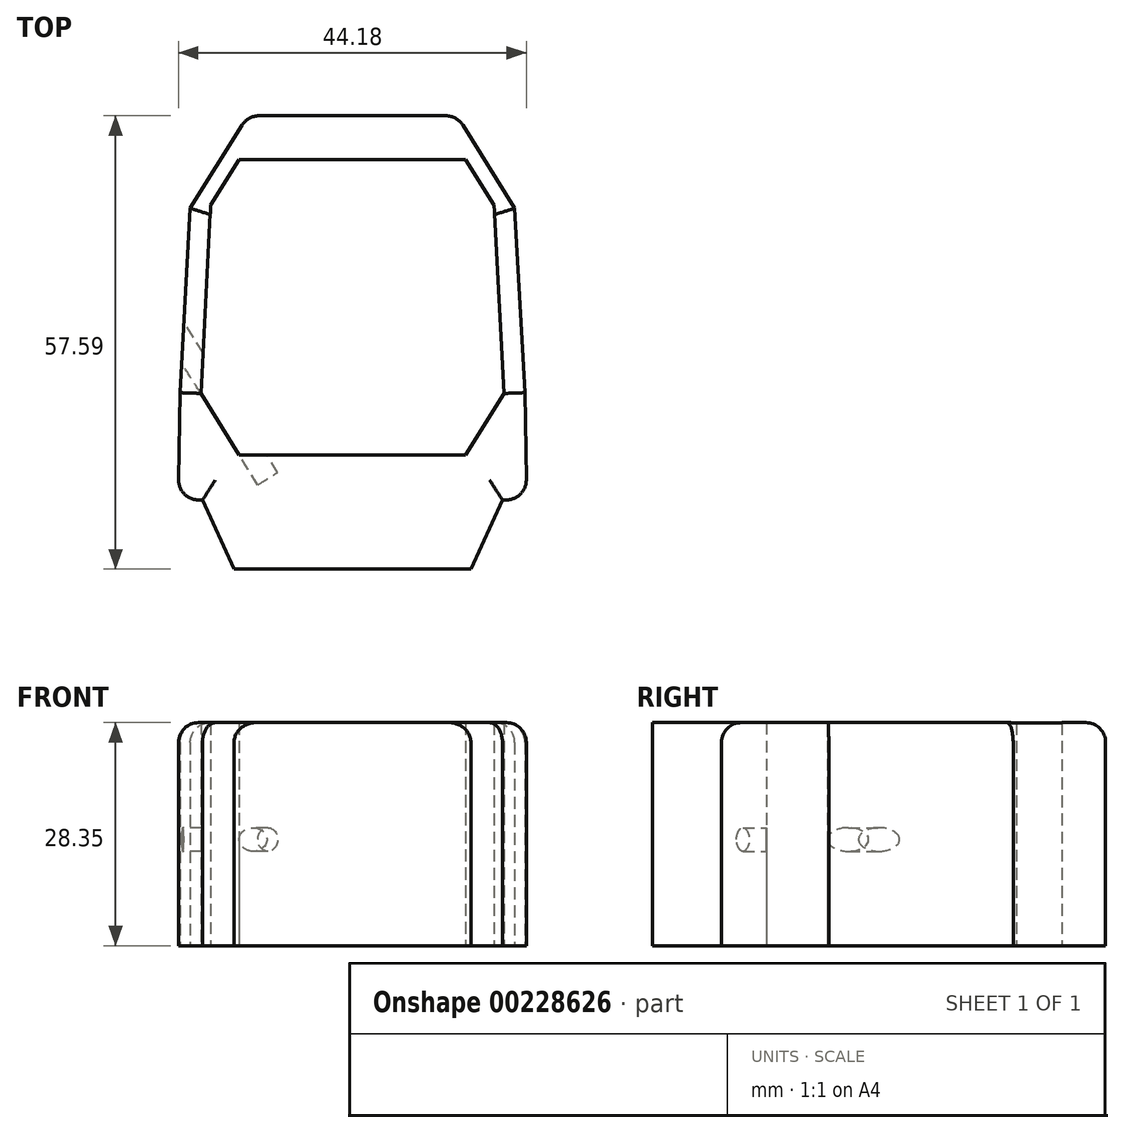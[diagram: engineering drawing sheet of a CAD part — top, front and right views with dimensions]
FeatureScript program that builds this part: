
annotation { "Feature Type Name" : "Feature", "Feature Type Description" : "" }
export const myFeature = defineFeature(function(context is Context, id is Id, definition is map)
    precondition{}
    {
        {
            var Q0;
            Q0=qCreatedBy(makeId("Top.planeOp"),FACE);
            var sketch = newSketch(context, id + "F0", { "sketchPlane" : qUnion([Q0])});
            skLineSegment(sketch, "E0", {"start": v(-14.4, -18.75) * mm, "end": v(14.4, -18.75) * mm});
            skLineSegment(sketch, "E1", {"start": v(14.4, -18.75) * mm, "end": v(19.25, -10.98) * mm});
            skLineSegment(sketch, "E2", {"start": v(19.25, -10.98) * mm, "end": v(18, 12.99) * mm});
            skLineSegment(sketch, "E3", {"start": v(18, 12.99) * mm, "end": v(14.4, 18.75) * mm});
            skLineSegment(sketch, "E4", {"start": v(14.4, 18.75) * mm, "end": v(-14.4, 18.75) * mm});
            skLineSegment(sketch, "E5", {"start": v(-14.4, 18.75) * mm, "end": v(-18, 12.99) * mm});
            skLineSegment(sketch, "E6", {"start": v(-18, 12.99) * mm, "end": v(-19.25, -10.98) * mm});
            skLineSegment(sketch, "E7", {"start": v(-19.25, -10.98) * mm, "end": v(-14.4, -18.75) * mm});
            skLineSegment(sketch, "E8", {"start": v(-15.04, -33.25) * mm, "end": v(15.04, -33.25) * mm});
            skLineSegment(sketch, "E9", {"start": v(22.13, -24.46) * mm, "end": v(21.92, -10.84) * mm});
            skLineSegment(sketch, "E10", {"start": v(13.27, 24.34) * mm, "end": v(-13.27, 24.34) * mm});
            skLineSegment(sketch, "E11", {"start": v(18, 12.99) * mm, "end": v(20.58, 13.12) * mm, "construction": true});
            skLineSegment(sketch, "E12", {"start": v(19.25, -10.98) * mm, "end": v(21.92, -10.84) * mm, "construction": true});
            skLineSegment(sketch, "E13", {"start": v(20.58, 13.12) * mm, "end": v(21.92, -10.84) * mm});
            skLineSegment(sketch, "E14", {"start": v(13.27, 24.34) * mm, "end": v(20.61, 12.6) * mm});
            skLineSegment(sketch, "E15.MirrorCS", {"start": v(-22.13, -24.46) * mm, "end": v(-21.92, -10.84) * mm});
            skLineSegment(sketch, "E16.MirrorCS", {"start": v(-13.27, 24.34) * mm, "end": v(-20.61, 12.6) * mm});
            skLineSegment(sketch, "E17.MirrorCS", {"start": v(-20.58, 13.12) * mm, "end": v(-21.92, -10.84) * mm});
            skLineSegment(sketch, "E18", {"start": v(19.05, -24.46) * mm, "end": v(22.13, -24.46) * mm});
            skLineSegment(sketch, "E19.MirrorCS", {"start": v(-19.05, -24.46) * mm, "end": v(-22.13, -24.46) * mm});
            skLineSegment(sketch, "E20", {"start": v(15.04, -33.25) * mm, "end": v(19.05, -24.46) * mm});
            skLineSegment(sketch, "E21", {"start": v(-15.04, -33.25) * mm, "end": v(-19.05, -24.46) * mm});
            skSolve(sketch);
        }
        {
            var Q0;
            Q0=makeQuery(id+"F0.imprint","IMPRINT",FACE,{"disambiguationData":[TD([[makeQuery(id+"F0.imprint","IMPRINT",EDGE,{"derivedFrom":sQuery(id+"F0.wireOp",EDGE,"E0")}),-1.0]])]});
            extrude(context, id + "F1", {"entities" : qUnion([Q0]), "depth" : 28.35 * mm});
        }
        {
            var Q0;
            Q0=qCreatedBy(makeId("Top.planeOp"),FACE);
            cPlane(context, id + "F2", {"entities" : qUnion([Q0]), "cplaneType" : CPlaneType.OFFSET, "offset" : 13.5 * mm, "width" : 150 * mm, "height" : 150 * mm});
        }
        {
            var Q0;
            Q0=qCreatedBy(id+"F2.planeOp",FACE);
            var sketch = newSketch(context, id + "F3", { "sketchPlane" : qUnion([Q0])});
            skLineSegment(sketch, "E22.0", {"start": v(-19.25, -10.98) * mm, "end": v(-14.4, -18.75) * mm, "construction": true});
            skLineSegment(sketch, "E23.0", {"start": v(-15.04, -33.25) * mm, "end": v(15.04, -33.25) * mm, "construction": true});
            skLineSegment(sketch, "E24", {"start": v(-24, -0.55) * mm, "end": v(-3.56, -33.25) * mm, "construction": true});
            skLineSegment(sketch, "E25", {"start": v(-10.75, -21.75) * mm, "end": v(-12.02, -22.54) * mm});
            skLineSegment(sketch, "E26", {"start": v(-12.02, -22.54) * mm, "end": v(-25.27, -1.34) * mm});
            skLineSegment(sketch, "E27", {"start": v(-10.75, -21.75) * mm, "end": v(-24, -0.55) * mm});
            skLineSegment(sketch, "E28", {"start": v(-25.27, -1.34) * mm, "end": v(-24, -0.55) * mm});
            skSolve(sketch);
        }
        {
            var Q0;
            Q0=makeQuery(id+"F3.imprint","IMPRINT",FACE,{"disambiguationData":[TD([[makeQuery(id+"F3.imprint","IMPRINT",EDGE,{"derivedFrom":sQuery(id+"F3.wireOp",EDGE,"E25")}),-1.0]])]});
            var Q1;
            Q1=sQuery(id+"F3.wireOp",EDGE,"E24");
            revolve(context, id + "F4", {"operationType" : NewBodyOperationType.REMOVE, "entities" : qUnion([Q0]), "axis" : qUnion([Q1]), "revolveType" : RevolveType.FULL});
        }
        {
            var Q0;
            Q0=makeQuery(id+"F1.opExtrude","CAP_EDGE",EDGE,{"disambiguationData":[OSD([sQuery(id+"F0.wireOp",EDGE,"E21")])],"isStart":false});
            var Q1;
            Q1=makeQuery(id+"F1.opExtrude","CAP_EDGE",EDGE,{"disambiguationData":[OSD([sQuery(id+"F0.wireOp",EDGE,"E19.MirrorCS")])],"isStart":false});
            var Q2;
            Q2=makeQuery(id+"F1.opExtrude","CAP_EDGE",EDGE,{"disambiguationData":[OSD([sQuery(id+"F0.wireOp",EDGE,"E17.MirrorCS")])],"isStart":false});
            var Q3;
            Q3=makeQuery(id+"F1.opExtrude","CAP_EDGE",EDGE,{"disambiguationData":[OSD([sQuery(id+"F0.wireOp",EDGE,"E15.MirrorCS")])],"isStart":false});
            var Q4;
            Q4=makeQuery(id+"F1.opExtrude","CAP_EDGE",EDGE,{"disambiguationData":[OSD([sQuery(id+"F0.wireOp",EDGE,"E16.MirrorCS")])],"isStart":false});
            var Q5;
            Q5=makeQuery(id+"F1.opExtrude","CAP_EDGE",EDGE,{"disambiguationData":[OSD([sQuery(id+"F0.wireOp",EDGE,"E10")])],"isStart":false});
            var Q6;
            Q6=makeQuery(id+"F1.opExtrude","CAP_EDGE",EDGE,{"disambiguationData":[OSD([sQuery(id+"F0.wireOp",EDGE,"E14")])],"isStart":false});
            var Q7;
            Q7=makeQuery(id+"F1.opExtrude","CAP_EDGE",EDGE,{"disambiguationData":[OSD([sQuery(id+"F0.wireOp",EDGE,"E13")])],"isStart":false});
            var Q8;
            Q8=makeQuery(id+"F1.opExtrude","CAP_EDGE",EDGE,{"disambiguationData":[OSD([sQuery(id+"F0.wireOp",EDGE,"E9")])],"isStart":false});
            var Q9;
            Q9=makeQuery(id+"F1.opExtrude","CAP_EDGE",EDGE,{"disambiguationData":[OSD([sQuery(id+"F0.wireOp",EDGE,"E18")])],"isStart":false});
            var Q10;
            Q10=makeQuery(id+"F1.opExtrude","CAP_EDGE",EDGE,{"disambiguationData":[OSD([sQuery(id+"F0.wireOp",EDGE,"E20")])],"isStart":false});
            fillet(context, id + "F5", {"entities" : qUnion([Q0, Q1, Q2, Q3, Q4, Q5, Q6, Q7, Q8, Q9, Q10]), "radius" : 2.54 * mm, "tangentPropagation" : true, "allowEdgeOverflow" : false});
        }
        {
            var Q0;
            Q0=makeQuery(id+"F5.opFillet","BLEND_EDGE",EDGE,{"blendedFrom":[makeQuery(id+"F1.opExtrude","CAP_EDGE",EDGE,{"disambiguationData":[OSD([sQuery(id+"F0.wireOp",EDGE,"E9")])],"isStart":false}),makeQuery(id+"F1.opExtrude","CAP_EDGE",EDGE,{"disambiguationData":[OSD([sQuery(id+"F0.wireOp",EDGE,"E18")])],"isStart":false})],"blendedInto":[]});
            var Q1;
            Q1=makeQuery(id+"F5.opFillet","BLEND_EDGE",EDGE,{"blendedFrom":[makeQuery(id+"F1.opExtrude","CAP_EDGE",EDGE,{"disambiguationData":[OSD([sQuery(id+"F0.wireOp",EDGE,"E15.MirrorCS")])],"isStart":false}),makeQuery(id+"F1.opExtrude","CAP_EDGE",EDGE,{"disambiguationData":[OSD([sQuery(id+"F0.wireOp",EDGE,"E19.MirrorCS")])],"isStart":false})],"blendedInto":[]});
            var Q2;
            Q2=makeQuery(id+"F5.opFillet","BLEND_EDGE",EDGE,{"blendedFrom":[makeQuery(id+"F1.opExtrude","CAP_EDGE",EDGE,{"disambiguationData":[OSD([sQuery(id+"F0.wireOp",EDGE,"E10")])],"isStart":false}),makeQuery(id+"F1.opExtrude","CAP_EDGE",EDGE,{"disambiguationData":[OSD([sQuery(id+"F0.wireOp",EDGE,"E16.MirrorCS")])],"isStart":false})],"blendedInto":[]});
            var Q3;
            Q3=makeQuery(id+"F5.opFillet","BLEND_EDGE",EDGE,{"blendedFrom":[makeQuery(id+"F1.opExtrude","CAP_EDGE",EDGE,{"disambiguationData":[OSD([sQuery(id+"F0.wireOp",EDGE,"E10")])],"isStart":false}),makeQuery(id+"F1.opExtrude","CAP_EDGE",EDGE,{"disambiguationData":[OSD([sQuery(id+"F0.wireOp",EDGE,"E14")])],"isStart":false})],"blendedInto":[]});
            fillet(context, id + "F6", {"entities" : qUnion([Q0, Q1, Q2, Q3]), "radius" : 2.54 * mm, "tangentPropagation" : true, "allowEdgeOverflow" : false});
        }
    });
